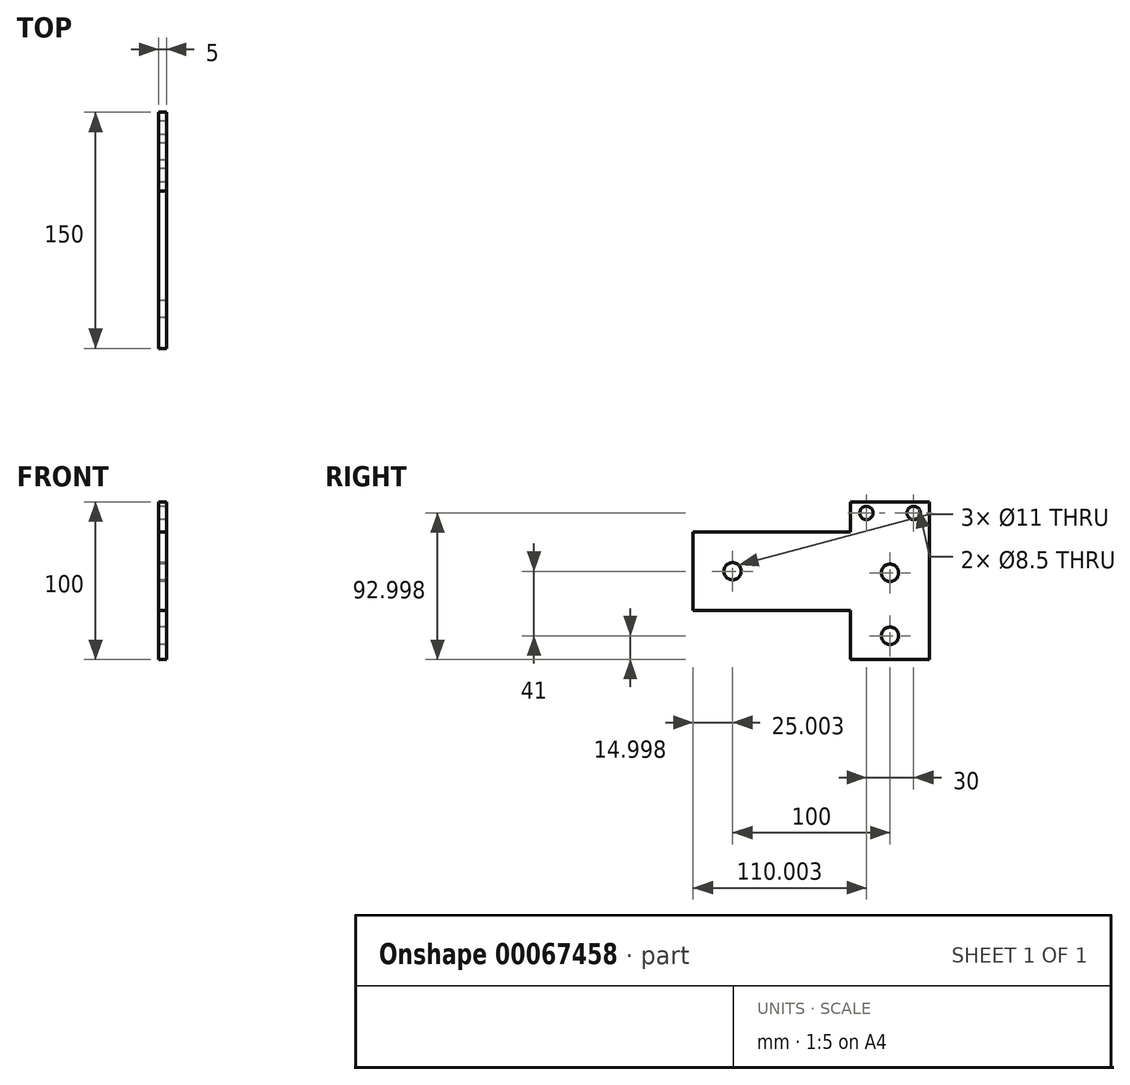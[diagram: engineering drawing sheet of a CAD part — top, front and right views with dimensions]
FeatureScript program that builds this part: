
annotation { "Feature Type Name" : "Feature", "Feature Type Description" : "" }
export const myFeature = defineFeature(function(context is Context, id is Id, definition is map)
    precondition{}
    {
        {
            var Q0;
            Q0=qCreatedBy(makeId("Right.planeOp"),FACE);
            var sketch = newSketch(context, id + "F0", { "sketchPlane" : qUnion([Q0])});
            skLineSegment(sketch, "E0.bottom", {"start": v(-18.97, 74.68) * mm, "end": v(31.03, 74.68) * mm});
            skLineSegment(sketch, "E0.top", {"start": v(-18.97, -25.32) * mm, "end": v(31.03, -25.32) * mm});
            skLineSegment(sketch, "E0.left", {"start": v(-18.97, 74.68) * mm, "end": v(-18.97, 55.68) * mm});
            skLineSegment(sketch, "E0.right", {"start": v(31.03, 74.68) * mm, "end": v(31.03, -25.32) * mm});
            skLineSegment(sketch, "E1.bottom", {"start": v(-18.97, 55.68) * mm, "end": v(-118.97, 55.68) * mm});
            skLineSegment(sketch, "E1.top", {"start": v(-18.97, 5.68) * mm, "end": v(-118.97, 5.68) * mm});
            skLineSegment(sketch, "E1.right", {"start": v(-118.97, 55.68) * mm, "end": v(-118.97, 5.68) * mm});
            skLineSegment(sketch, "E2.trimOffspring", {"start": v(-18.97, 5.68) * mm, "end": v(-18.97, -25.32) * mm});
            skPoint(sketch, "E3", {"position": v(-8.97, 67.68) * mm});
            skPoint(sketch, "E4", {"position": v(21.03, 67.68) * mm});
            skPoint(sketch, "E5", {"position": v(-93.97, 30.68) * mm});
            skPoint(sketch, "E6", {"position": v(6.03, -10.32) * mm});
            skPoint(sketch, "E7", {"position": v(6.03, 29.68) * mm});
            skSolve(sketch);
        }
        {
            var Q0;
            Q0 = qSketchRegion(id + "F0", true);
            extrude(context, id + "F1", {"entities" : qUnion([Q0]), "depth" : 5 * mm});
        }
        {
            var Q0;
            Q0=sQuery(id+"F0.wireOp",VERTEX,"E3");
            var Q1;
            Q1=sQuery(id+"F0.wireOp",VERTEX,"E4");
            var Q2;
            Q2=makeQuery(id+"F1.opExtrude","SWEPT_BODY",BODY,{"disambiguationData":[OSD([sQuery(id+"F0.wireOp",EDGE,"E0.bottom"),sQuery(id+"F0.wireOp",EDGE,"E0.top"),sQuery(id+"F0.wireOp",EDGE,"E0.left"),sQuery(id+"F0.wireOp",EDGE,"E0.right"),sQuery(id+"F0.wireOp",EDGE,"E1.bottom"),sQuery(id+"F0.wireOp",EDGE,"E1.top"),sQuery(id+"F0.wireOp",EDGE,"E1.right"),sQuery(id+"F0.wireOp",EDGE,"E2.trimOffspring")])]});
            hole(context, id + "F2", {"style" : HoleStyle.SIMPLE, "holeDiameter" : 8.5 * mm, "endStyle" : HoleEndStyle.THROUGH, "oppositeDirection" : true, "locations" : qUnion([Q0, Q1]), "scope" : qUnion([Q2])});
        }
        {
            var Q0;
            Q0=sQuery(id+"F0.wireOp",VERTEX,"E7");
            var Q1;
            Q1=sQuery(id+"F0.wireOp",VERTEX,"E6");
            var Q2;
            Q2=sQuery(id+"F0.wireOp",VERTEX,"13c7d7bb-7ee1-4f64-9a06-82743bb3aed4");
            var Q3;
            Q3=sQuery(id+"F0.wireOp",VERTEX,"E5");
            var Q4;
            Q4=makeQuery(id+"F1.opExtrude","SWEPT_BODY",BODY,{"disambiguationData":[OSD([sQuery(id+"F0.wireOp",EDGE,"E0.bottom"),sQuery(id+"F0.wireOp",EDGE,"E0.top"),sQuery(id+"F0.wireOp",EDGE,"E0.left"),sQuery(id+"F0.wireOp",EDGE,"E0.right"),sQuery(id+"F0.wireOp",EDGE,"E1.bottom"),sQuery(id+"F0.wireOp",EDGE,"E1.top"),sQuery(id+"F0.wireOp",EDGE,"E1.right"),sQuery(id+"F0.wireOp",EDGE,"E2.trimOffspring")])]});
            hole(context, id + "F3", {"style" : HoleStyle.SIMPLE, "holeDiameter" : 11 * mm, "endStyle" : HoleEndStyle.THROUGH, "oppositeDirection" : true, "locations" : qUnion([Q0, Q1, Q2, Q3]), "scope" : qUnion([Q4])});
        }
    });
